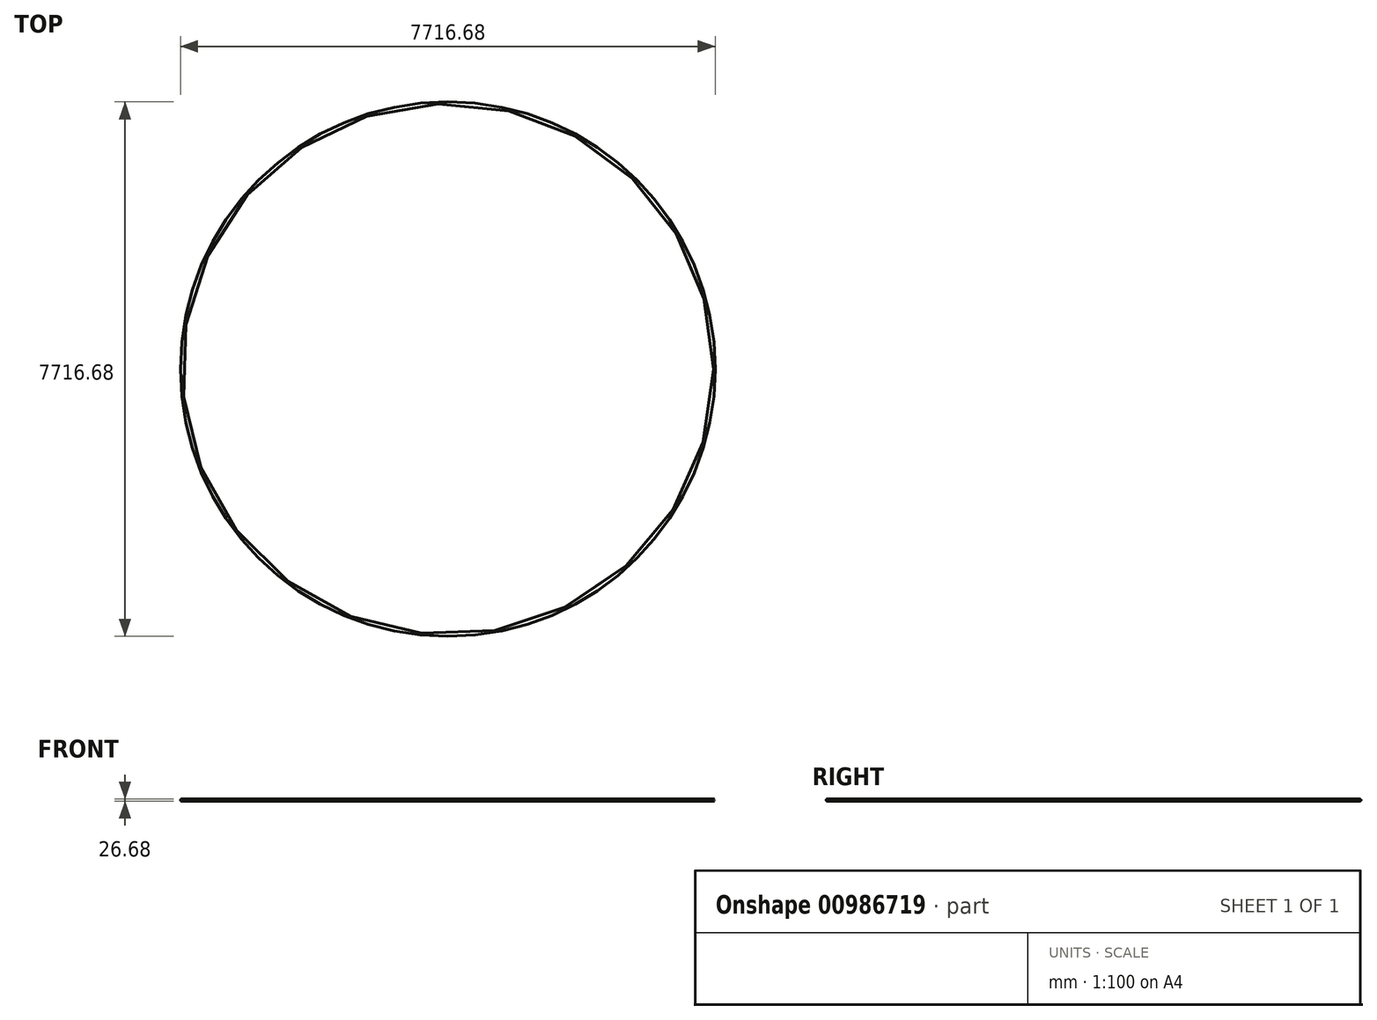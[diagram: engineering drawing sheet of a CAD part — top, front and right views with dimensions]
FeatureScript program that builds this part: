
annotation { "Feature Type Name" : "Feature", "Feature Type Description" : "" }
export const myFeature = defineFeature(function(context is Context, id is Id, definition is map)
    precondition{}
    {
        {
            var Q0;
            Q0=qCreatedBy(makeId("Front.planeOp"),FACE);
            var sketch = newSketch(context, id + "F0", { "sketchPlane" : qUnion([Q0])});
            skLineSegment(sketch, "E0", {"start": v(0, 0) * mm, "end": v(3845, 0) * mm, "construction": true});
            skLineSegment(sketch, "E1", {"start": v(3845, 0) * mm, "end": v(3845, -100) * mm, "construction": true});
            skCircle(sketch, "E2", {"center": v(0, 0) * mm, "radius": 13.34 * mm});
            skCircle(sketch, "E3.0", {"center": v(0, 0) * mm, "radius": 11.23 * mm});
            skSolve(sketch);
        }
        {
            var Q0;
            Q0 = qSketchRegion(id + "F0", true);
            var Q1;
            Q1=sQuery(id+"F0.wireOp",EDGE,"E1");
            revolve(context, id + "F1", {"surfaceOperationType" : NewSurfaceOperationType.NEW, "entities" : qUnion([Q0]), "axis" : qUnion([Q1]), "revolveType" : RevolveType.FULL});
        }
    });
